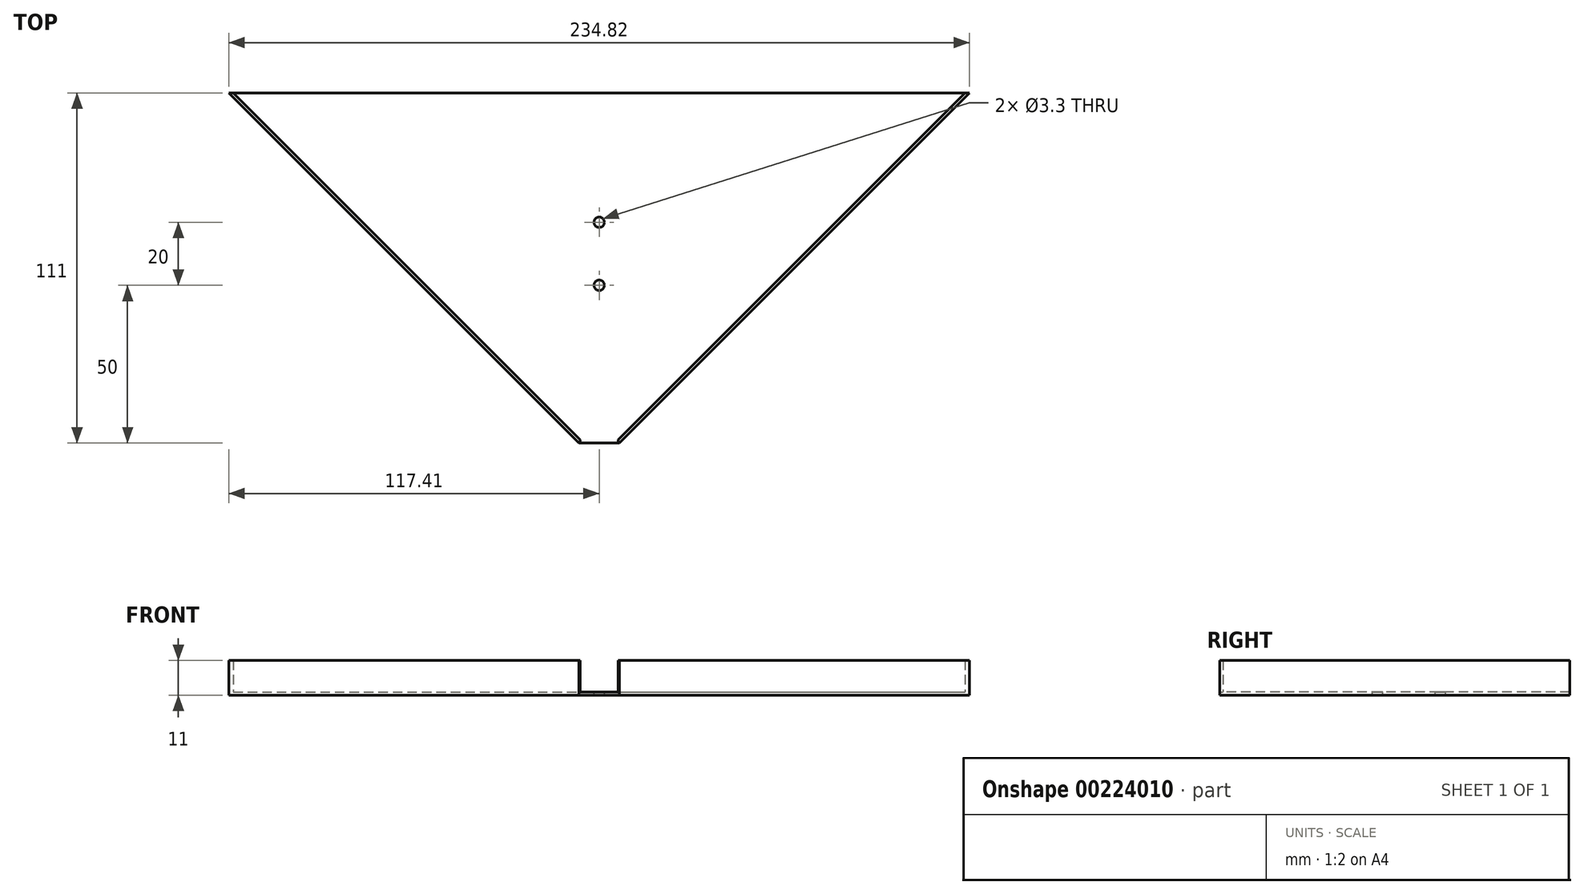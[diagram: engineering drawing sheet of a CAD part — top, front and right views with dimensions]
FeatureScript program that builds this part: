
annotation { "Feature Type Name" : "Feature", "Feature Type Description" : "" }
export const myFeature = defineFeature(function(context is Context, id is Id, definition is map)
    precondition{}
    {
        {
            var Q0;
            Q0=qCreatedBy(makeId("Top.planeOp"),FACE);
            var sketch = newSketch(context, id + "F0", { "sketchPlane" : qUnion([Q0])});
            skLineSegment(sketch, "E0", {"start": v(-116, 0) * mm, "end": v(-6, -110) * mm});
            skLineSegment(sketch, "E1", {"start": v(6, -110) * mm, "end": v(116, 0) * mm});
            skLineSegment(sketch, "E2", {"start": v(-116, 0) * mm, "end": v(116, 0) * mm});
            skLineSegment(sketch, "E3", {"start": v(-6, -110) * mm, "end": v(6, -110) * mm});
            skSolve(sketch);
        }
        {
            var Q0;
            Q0 = qSketchRegion(id + "F0", true);
            extrude(context, id + "F1", {"entities" : qUnion([Q0]), "depth" : 10 * mm});
        }
        {
            var Q0;
            Q0=makeQuery(id+"F1.opExtrude","CAP_FACE",FACE,{"disambiguationData":[OSD([sQuery(id+"F0.wireOp",EDGE,"JIZEV4Tr-e6P4-xHz4-srPp-dx90MIWAYZKB.bottom"),sQuery(id+"F0.wireOp",EDGE,"JIZEV4Tr-e6P4-xHz4-srPp-dx90MIWAYZKB.left"),sQuery(id+"F0.wireOp",EDGE,"JIZEV4Tr-e6P4-xHz4-srPp-dx90MIWAYZKB.right"),sQuery(id+"F0.wireOp",EDGE,"E0"),sQuery(id+"F0.wireOp",EDGE,"E1"),sQuery(id+"F0.wireOp",EDGE,"T4RzTtzX-cZbX-pctD-1qud-cGSIHwkOpFI1"),sQuery(id+"F0.wireOp",EDGE,"VnKgwsDQ-Tgki-ny5G-jk61-1Z1qphEyjRAN"),sQuery(id+"F0.wireOp",EDGE,"xSV0rPfs-aLod-2Jib-Q2NB-3cvwirHivi60")])],"isStart":false});
            var Q1;
            Q1=makeQuery(id+"F1.opExtrude","SWEPT_BODY",BODY,{"disambiguationData":[OSD([sQuery(id+"F0.wireOp",EDGE,"JIZEV4Tr-e6P4-xHz4-srPp-dx90MIWAYZKB.bottom"),sQuery(id+"F0.wireOp",EDGE,"JIZEV4Tr-e6P4-xHz4-srPp-dx90MIWAYZKB.left"),sQuery(id+"F0.wireOp",EDGE,"JIZEV4Tr-e6P4-xHz4-srPp-dx90MIWAYZKB.right"),sQuery(id+"F0.wireOp",EDGE,"E0"),sQuery(id+"F0.wireOp",EDGE,"E1"),sQuery(id+"F0.wireOp",EDGE,"T4RzTtzX-cZbX-pctD-1qud-cGSIHwkOpFI1"),sQuery(id+"F0.wireOp",EDGE,"VnKgwsDQ-Tgki-ny5G-jk61-1Z1qphEyjRAN"),sQuery(id+"F0.wireOp",EDGE,"xSV0rPfs-aLod-2Jib-Q2NB-3cvwirHivi60")])]});
            shell(context, id + "F2", {"entities" : qUnion([Q0]), "parts" : qUnion([Q1]), "thickness" : 1 * mm, "oppositeDirection" : true});
        }
        {
            var Q0;
            Q0=makeQuery(id+"F2.opShell","OFFSET_FACE",FACE,{"disambiguationData":[OSD([sQuery(id+"F0.wireOp",EDGE,"E3")])]});
            var sketch = newSketch(context, id + "F3", { "sketchPlane" : qUnion([Q0])});
            skLineSegment(sketch, "E4.bottom", {"start": v(6, 10) * mm, "end": v(-6, 10) * mm});
            skLineSegment(sketch, "E4.top", {"start": v(6, 0) * mm, "end": v(-6, 0) * mm});
            skLineSegment(sketch, "E4.left", {"start": v(6, 10) * mm, "end": v(6, 0) * mm});
            skLineSegment(sketch, "E4.right", {"start": v(-6, 10) * mm, "end": v(-6, 0) * mm});
            skSolve(sketch);
        }
        {
            var Q0;
            Q0 = qSketchRegion(id + "F3", true);
            extrude(context, id + "F4", {"entities" : qUnion([Q0]), "operationType" : NewBodyOperationType.REMOVE, "oppositeDirection" : true, "depth" : 25 * mm});
        }
        {
            var Q0;
            Q0=makeQuery(id+"F1.opExtrude","SWEPT_FACE",FACE,{"disambiguationData":[OSD([sQuery(id+"F0.wireOp",EDGE,"E2")])]});
            var sketch = newSketch(context, id + "F5", { "sketchPlane" : qUnion([Q0])});
            skLineSegment(sketch, "E5.bottom", {"start": v(-118.41, 10) * mm, "end": v(118.41, 10) * mm});
            skLineSegment(sketch, "E5.top", {"start": v(-118.41, -1) * mm, "end": v(118.41, -1) * mm});
            skLineSegment(sketch, "E5.left", {"start": v(-118.41, 10) * mm, "end": v(-118.41, -1) * mm});
            skLineSegment(sketch, "E5.right", {"start": v(118.41, 10) * mm, "end": v(118.41, -1) * mm});
            skSolve(sketch);
        }
        {
            var Q0;
            Q0 = qSketchRegion(id + "F5", true);
            extrude(context, id + "F6", {"entities" : qUnion([Q0]), "operationType" : NewBodyOperationType.REMOVE, "oppositeDirection" : true, "depth" : 1 * mm});
        }
        {
            var Q0;
            Q0=makeQuery(id+"F4.boolean.opBoolean","MERGE",FACE,{"derivedFrom":[makeQuery(id+"F2.opShell","OFFSET_FACE",FACE,{"disambiguationData":[OSD([sQuery(id+"F0.wireOp",EDGE,"E0"),sQuery(id+"F0.wireOp",EDGE,"E1"),sQuery(id+"F0.wireOp",EDGE,"E2"),sQuery(id+"F0.wireOp",EDGE,"E3")])]}),makeQuery(id+"F4.opExtrude","SWEPT_FACE",FACE,{"disambiguationData":[OSD([sQuery(id+"F3.wireOp",EDGE,"E4.top")])]})]});
            var sketch = newSketch(context, id + "F7", { "sketchPlane" : qUnion([Q0])});
            skPoint(sketch, "E6.positionSnap0", {"position": v(0, 0) * mm});
            skPoint(sketch, "E7", {"position": v(0, -41) * mm});
            skPoint(sketch, "E8", {"position": v(0, -61) * mm});
            skSolve(sketch);
        }
        {
            var Q0;
            Q0=sQuery(id+"F7.wireOp",VERTEX,"E7");
            var Q1;
            Q1=sQuery(id+"F7.wireOp",VERTEX,"E8");
            var Q2;
            Q2=makeQuery(id+"F1.opExtrude","SWEPT_BODY",BODY,{"disambiguationData":[OSD([sQuery(id+"F0.wireOp",EDGE,"E0"),sQuery(id+"F0.wireOp",EDGE,"E1"),sQuery(id+"F0.wireOp",EDGE,"E2"),sQuery(id+"F0.wireOp",EDGE,"E3")])]});
            hole(context, id + "F8", {"style" : HoleStyle.SIMPLE, "endStyle" : HoleEndStyle.THROUGH, "standardTappedOrClearance" : lookupTablePath({ "standard" : "ISO", "fit" : "Normal", "size" : "M3", "type" : "Clearance" }), "standardBlindInLast" : lookupTablePath({ "fit" : "Standard", "standard" : "ISO", "size" : "M3", "type" : "Clearance" }), "holeDiameter" : 3.3 * mm, "locations" : qUnion([Q0, Q1]), "scope" : qUnion([Q2]), "tappedDepth" : 12 * mm, "tapClearance" : 3});
        }
    });
